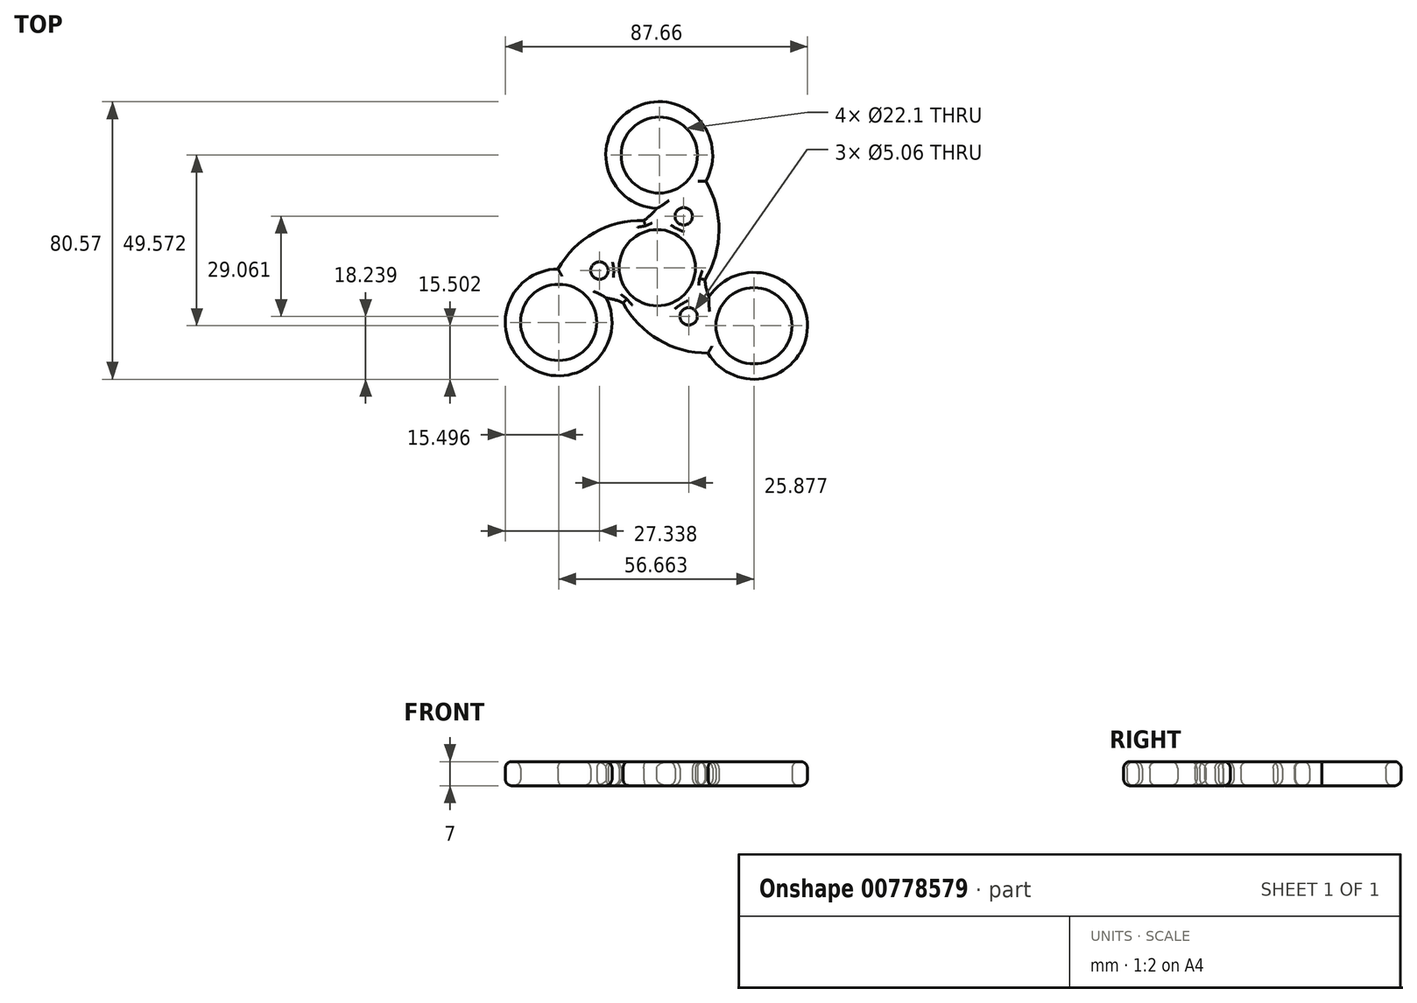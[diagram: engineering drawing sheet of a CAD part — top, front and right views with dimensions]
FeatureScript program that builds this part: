
annotation { "Feature Type Name" : "Feature", "Feature Type Description" : "" }
export const myFeature = defineFeature(function(context is Context, id is Id, definition is map)
    precondition{}
    {
        {
            var Q0;
            Q0=qCreatedBy(makeId("Top.planeOp"),FACE);
            var sketch = newSketch(context, id + "F0", { "sketchPlane" : qUnion([Q0])});
            skCircle(sketch, "E0", {"center": v(-20.85, 25.1) * mm, "radius": 11.05 * mm});
            skArc(sketch, "E1", {"start": v(-30.79, 14.88) * mm, "mid": v(-20.48, 4.2) * mm, "end": v(-6.14, 0.34) * mm});
            skArc(sketch, "E2", {"start": v(-7.03, 21.62) * mm, "mid": v(-6.64, 19.1) * mm, "end": v(-5.83, 16.67) * mm});
            skCircle(sketch, "E3", {"center": v(7.19, 8.25) * mm, "radius": 11.05 * mm});
            skArc(sketch, "E4", {"start": v(-6.14, 0.34) * mm, "mid": v(22.69, 7.96) * mm, "end": v(-5.83, 16.67) * mm});
            skArc(sketch, "E5.1.0", {"start": v(-24.74, 38.83) * mm, "mid": v(-22.75, 40.43) * mm, "end": v(-21.06, 42.34) * mm});
            skCircle(sketch, "E5.1.1", {"center": v(-20.28, 57.82) * mm, "radius": 11.05 * mm});
            skArc(sketch, "E5.1.2", {"start": v(-6.76, 50.24) * mm, "mid": v(-27.77, 71.4) * mm, "end": v(-21.06, 42.34) * mm});
            skArc(sketch, "E5.1.3", {"start": v(-7.03, 21.62) * mm, "mid": v(-2.94, 35.9) * mm, "end": v(-6.76, 50.24) * mm});
            skArc(sketch, "E5.2.0", {"start": v(-30.79, 14.88) * mm, "mid": v(-33.17, 15.8) * mm, "end": v(-35.68, 16.32) * mm});
            skCircle(sketch, "E5.2.1", {"center": v(-49.47, 9.25) * mm, "radius": 11.05 * mm});
            skArc(sketch, "E5.2.2", {"start": v(-49.66, 24.75) * mm, "mid": v(-57.48, -4.02) * mm, "end": v(-35.68, 16.32) * mm});
            skArc(sketch, "E5.2.3", {"start": v(-24.74, 38.83) * mm, "mid": v(-39.15, 35.24) * mm, "end": v(-49.66, 24.75) * mm});
            skPoint(sketch, "E6.trimOffspring.end.orphan", {"position": v(-6.85, 25.1) * mm});
            skPoint(sketch, "E7.orphan", {"position": v(-7.52, 20.85) * mm});
            skPoint(sketch, "E8.orphan", {"position": v(-27.85, 37.23) * mm});
            skPoint(sketch, "E9.orphan", {"position": v(-23.83, 38.79) * mm});
            skCircle(sketch, "E10", {"center": v(-13.17, 40.05) * mm, "radius": 2.53 * mm});
            skCircle(sketch, "E11.1.0", {"center": v(-37.63, 24.3) * mm, "radius": 2.53 * mm});
            skCircle(sketch, "E11.2.0", {"center": v(-11.75, 10.99) * mm, "radius": 2.53 * mm});
            skSolve(sketch);
        }
        {
            var Q0;
            Q0 = qSketchRegion(id + "F0", true);
            extrude(context, id + "F1", {"entities" : qUnion([Q0]), "depth" : 7 * mm, "offsetDistance" : 25 * mm});
        }
        {
            var Q0;
            Q0=makeQuery(id+"F1.opExtrude","CAP_EDGE",EDGE,{"disambiguationData":[OSD([sQuery(id+"F0.wireOp",EDGE,"E5.2.1")])],"isStart":false});
            var Q1;
            Q1=makeQuery(id+"F1.opExtrude","CAP_EDGE",EDGE,{"disambiguationData":[OSD([sQuery(id+"F0.wireOp",EDGE,"E5.2.2")])],"isStart":false});
            var Q2;
            Q2=makeQuery(id+"F1.opExtrude","CAP_EDGE",EDGE,{"disambiguationData":[OSD([sQuery(id+"F0.wireOp",EDGE,"E5.2.2")])],"isStart":true});
            var Q3;
            Q3=makeQuery(id+"F1.opExtrude","CAP_EDGE",EDGE,{"disambiguationData":[OSD([sQuery(id+"F0.wireOp",EDGE,"E5.2.0")])],"isStart":false});
            var Q4;
            Q4=makeQuery(id+"F1.opExtrude","CAP_EDGE",EDGE,{"disambiguationData":[OSD([sQuery(id+"F0.wireOp",EDGE,"E5.2.0")])],"isStart":true});
            var Q5;
            Q5=makeQuery(id+"F1.opExtrude","CAP_EDGE",EDGE,{"disambiguationData":[OSD([sQuery(id+"F0.wireOp",EDGE,"E1")])],"isStart":true});
            var Q6;
            Q6=makeQuery(id+"F1.opExtrude","CAP_EDGE",EDGE,{"disambiguationData":[OSD([sQuery(id+"F0.wireOp",EDGE,"E1")])],"isStart":false});
            var Q7;
            Q7=makeQuery(id+"F1.opExtrude","CAP_EDGE",EDGE,{"disambiguationData":[OSD([sQuery(id+"F0.wireOp",EDGE,"E4")])],"isStart":false});
            var Q8;
            Q8=makeQuery(id+"F1.opExtrude","CAP_EDGE",EDGE,{"disambiguationData":[OSD([sQuery(id+"F0.wireOp",EDGE,"E4")])],"isStart":true});
            var Q9;
            Q9=makeQuery(id+"F1.opExtrude","CAP_EDGE",EDGE,{"disambiguationData":[OSD([sQuery(id+"F0.wireOp",EDGE,"E2")])],"isStart":false});
            var Q10;
            Q10=makeQuery(id+"F1.opExtrude","CAP_EDGE",EDGE,{"disambiguationData":[OSD([sQuery(id+"F0.wireOp",EDGE,"E3")])],"isStart":true});
            var Q11;
            Q11=makeQuery(id+"F1.opExtrude","CAP_EDGE",EDGE,{"disambiguationData":[OSD([sQuery(id+"F0.wireOp",EDGE,"E2")])],"isStart":true});
            var Q12;
            Q12=makeQuery(id+"F1.opExtrude","CAP_EDGE",EDGE,{"disambiguationData":[OSD([sQuery(id+"F0.wireOp",EDGE,"E5.1.3")])],"isStart":true});
            var Q13;
            Q13=makeQuery(id+"F1.opExtrude","CAP_EDGE",EDGE,{"disambiguationData":[OSD([sQuery(id+"F0.wireOp",EDGE,"E5.2.3")])],"isStart":false});
            var Q14;
            Q14=makeQuery(id+"F1.opExtrude","CAP_EDGE",EDGE,{"disambiguationData":[OSD([sQuery(id+"F0.wireOp",EDGE,"E5.2.3")])],"isStart":true});
            var Q15;
            Q15=makeQuery(id+"F1.opExtrude","CAP_EDGE",EDGE,{"disambiguationData":[OSD([sQuery(id+"F0.wireOp",EDGE,"E5.1.0")])],"isStart":true});
            var Q16;
            Q16=makeQuery(id+"F1.opExtrude","CAP_EDGE",EDGE,{"disambiguationData":[OSD([sQuery(id+"F0.wireOp",EDGE,"E5.1.0")])],"isStart":false});
            var Q17;
            Q17=makeQuery(id+"F1.opExtrude","CAP_EDGE",EDGE,{"disambiguationData":[OSD([sQuery(id+"F0.wireOp",EDGE,"E5.1.2")])],"isStart":false});
            var Q18;
            Q18=makeQuery(id+"F1.opExtrude","CAP_EDGE",EDGE,{"disambiguationData":[OSD([sQuery(id+"F0.wireOp",EDGE,"E5.1.1")])],"isStart":false});
            var Q19;
            Q19=makeQuery(id+"F1.opExtrude","CAP_EDGE",EDGE,{"disambiguationData":[OSD([sQuery(id+"F0.wireOp",EDGE,"E5.1.2")])],"isStart":true});
            var Q20;
            Q20=makeQuery(id+"F1.opExtrude","CAP_EDGE",EDGE,{"disambiguationData":[OSD([sQuery(id+"F0.wireOp",EDGE,"E5.1.3")])],"isStart":false});
            var Q21;
            Q21=makeQuery(id+"F1.opExtrude","CAP_EDGE",EDGE,{"disambiguationData":[OSD([sQuery(id+"F0.wireOp",EDGE,"E5.1.1")])],"isStart":true});
            var Q22;
            Q22=makeQuery(id+"F1.opExtrude","CAP_FACE",FACE,{"disambiguationData":[OSD([sQuery(id+"F0.wireOp",EDGE,"E0"),sQuery(id+"F0.wireOp",EDGE,"E1"),sQuery(id+"F0.wireOp",EDGE,"E2"),sQuery(id+"F0.wireOp",EDGE,"E3"),sQuery(id+"F0.wireOp",EDGE,"E4"),sQuery(id+"F0.wireOp",EDGE,"E5.1.0"),sQuery(id+"F0.wireOp",EDGE,"E5.1.1"),sQuery(id+"F0.wireOp",EDGE,"E5.1.2"),sQuery(id+"F0.wireOp",EDGE,"E5.1.3"),sQuery(id+"F0.wireOp",EDGE,"E5.2.0"),sQuery(id+"F0.wireOp",EDGE,"E5.2.1"),sQuery(id+"F0.wireOp",EDGE,"E5.2.2"),sQuery(id+"F0.wireOp",EDGE,"E5.2.3"),sQuery(id+"F0.wireOp",EDGE,"E10"),sQuery(id+"F0.wireOp",EDGE,"E11.1.0"),sQuery(id+"F0.wireOp",EDGE,"E11.2.0")])],"isStart":true});
            var Q23;
            Q23=makeQuery(id+"F1.opExtrude","CAP_FACE",FACE,{"disambiguationData":[OSD([sQuery(id+"F0.wireOp",EDGE,"E0"),sQuery(id+"F0.wireOp",EDGE,"E1"),sQuery(id+"F0.wireOp",EDGE,"E2"),sQuery(id+"F0.wireOp",EDGE,"E3"),sQuery(id+"F0.wireOp",EDGE,"E4"),sQuery(id+"F0.wireOp",EDGE,"E5.1.0"),sQuery(id+"F0.wireOp",EDGE,"E5.1.1"),sQuery(id+"F0.wireOp",EDGE,"E5.1.2"),sQuery(id+"F0.wireOp",EDGE,"E5.1.3"),sQuery(id+"F0.wireOp",EDGE,"E5.2.0"),sQuery(id+"F0.wireOp",EDGE,"E5.2.1"),sQuery(id+"F0.wireOp",EDGE,"E5.2.2"),sQuery(id+"F0.wireOp",EDGE,"E5.2.3"),sQuery(id+"F0.wireOp",EDGE,"E10"),sQuery(id+"F0.wireOp",EDGE,"E11.1.0"),sQuery(id+"F0.wireOp",EDGE,"E11.2.0")])],"isStart":false});
            fillet(context, id + "F2", {"entities" : qUnion([Q0, Q1, Q2, Q3, Q4, Q5, Q6, Q7, Q8, Q9, Q10, Q11, Q12, Q13, Q14, Q15, Q16, Q17, Q18, Q19, Q20, Q21, Q22, Q23]), "radius" : 2 * mm, "tangentPropagation" : true, "allowEdgeOverflow" : false});
        }
    });
